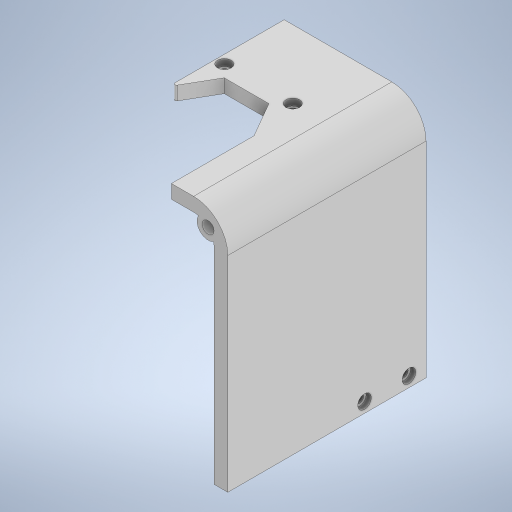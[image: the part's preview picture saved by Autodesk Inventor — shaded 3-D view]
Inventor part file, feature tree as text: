
AUTODESK INVENTOR PART (.ipt)
format: ipt  version: 2023 (Build 270158000, 158)  size: 342,016 bytes
history: native  units: mm
features: extrude x11, sketch x9, projected_geometry x2, other x1, fillet x1
ambient origin geometry x8: Origin, YZ Plane, XZ Plane, XY Plane, X Axis, Y Axis, Z Axis, Center Point
bodies: Body1 (feature_tree)
feature tree (24):
  other  "솔리드1"
  extrude  "돌출1"  Depth=70.0mm
  extrude  "돌출2"  Depth=41.5mm
  extrude  "돌출3"  Depth=4.0mm
  extrude  "돌출4"  TaperAngle=90.0deg  [1 undecoded]
  extrude  "돌출5"  Depth=6.0mm
  fillet  "모깎기2"  Radius=10.0mm
  sketch  "스케치6"
  extrude  "돌출6"  Depth=23.0mm TaperAngle=0.0deg
  extrude  "돌출7"  Depth=6.0mm
  sketch  "스케치7"
  extrude  "돌출8"  Depth=2.5mm
  extrude  "돌출9"  Depth=2.5mm
  extrude  "돌출10"  Depth=5.0mm
  extrude  "돌출11"  Depth=5.0mm
  sketch  "스케치1"
  sketch  "스케치2"
  sketch  "스케치3"
  sketch  "스케치4"
  sketch  "스케치5"
  projected_geometry  "투영된 루프1"
  sketch  "스케치8"
  sketch  "스케치9"
  projected_geometry  "투영된 루프2"
note: 1 required parameter value undecoded (feature->parameter linkage not recoverable at this tier; creation-order binding heuristic only, values carry confidence <= 0.55)
